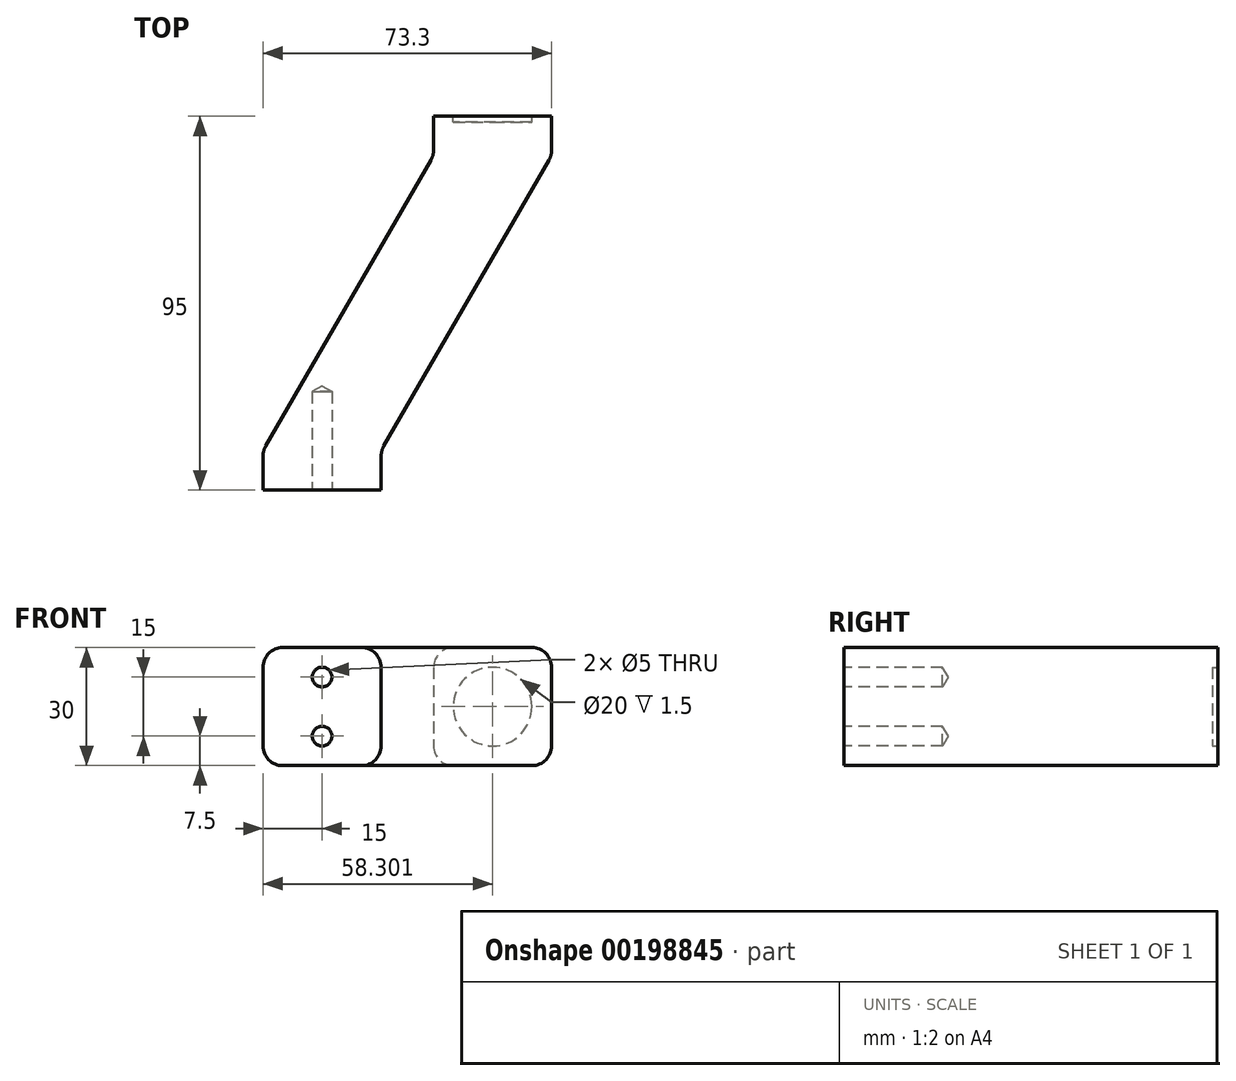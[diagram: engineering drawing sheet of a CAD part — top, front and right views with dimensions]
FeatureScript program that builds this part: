
annotation { "Feature Type Name" : "Feature", "Feature Type Description" : "" }
export const myFeature = defineFeature(function(context is Context, id is Id, definition is map)
    precondition{}
    {
        {
            var Q0;
            Q0=qCreatedBy(makeId("Top.planeOp"),FACE);
            var sketch = newSketch(context, id + "F0", { "sketchPlane" : qUnion([Q0])});
            skLineSegment(sketch, "E0.bottom", {"start": v(15, -5) * mm, "end": v(-15, -5) * mm});
            skLineSegment(sketch, "E0.top", {"start": v(15, 5) * mm, "end": v(-15, 5) * mm});
            skLineSegment(sketch, "E0.left", {"start": v(15, -5) * mm, "end": v(15, 5) * mm});
            skLineSegment(sketch, "E0.right", {"start": v(-15, -5) * mm, "end": v(-15, 5) * mm});
            skPoint(sketch, "E0.middle", {"position": v(0, 0) * mm});
            skLineSegment(sketch, "E1", {"start": v(15, 5) * mm, "end": v(58.3, 80) * mm});
            skLineSegment(sketch, "E2", {"start": v(-15, 5) * mm, "end": v(28.3, 80) * mm});
            skLineSegment(sketch, "E3.bottom", {"start": v(28.3, 80) * mm, "end": v(58.3, 80) * mm});
            skLineSegment(sketch, "E3.top", {"start": v(28.3, 90) * mm, "end": v(58.3, 90) * mm});
            skLineSegment(sketch, "E3.left", {"start": v(28.3, 80) * mm, "end": v(28.3, 90) * mm});
            skLineSegment(sketch, "E3.right", {"start": v(58.3, 80) * mm, "end": v(58.3, 90) * mm});
            skSolve(sketch);
        }
        {
            var Q0;
            Q0=makeQuery(id+"F0.imprint","IMPRINT",FACE,{"disambiguationData":[TD([[makeQuery(id+"F0.imprint","IMPRINT",EDGE,{"derivedFrom":sQuery(id+"F0.wireOp",EDGE,"E0.bottom")}),-1.0]])]});
            var Q1;
            Q1=makeQuery(id+"F0.imprint","IMPRINT",FACE,{"disambiguationData":[TD([[makeQuery(id+"F0.imprint","IMPRINT",EDGE,{"derivedFrom":sQuery(id+"F0.wireOp",EDGE,"E0.top")}),-1.0]])]});
            var Q2;
            Q2=makeQuery(id+"F0.imprint","IMPRINT",FACE,{"disambiguationData":[TD([[makeQuery(id+"F0.imprint","IMPRINT",EDGE,{"derivedFrom":sQuery(id+"F0.wireOp",EDGE,"E3.bottom")}),1.0]])]});
            extrude(context, id + "F1", {"entities" : qUnion([Q0, Q1, Q2]), "depth" : 30 * mm});
        }
        {
            var Q0;
            Q0=makeQuery(id+"F1.opExtrude","SWEPT_FACE",FACE,{"disambiguationData":[OSD([sQuery(id+"F0.wireOp",EDGE,"E0.bottom")])]});
            var sketch = newSketch(context, id + "F2", { "sketchPlane" : qUnion([Q0])});
            skPoint(sketch, "E4", {"position": v(0, 22.5) * mm});
            skPoint(sketch, "E4.positionSnap0", {"position": v(0, 30) * mm});
            skPoint(sketch, "E5", {"position": v(0, 7.5) * mm});
            skSolve(sketch);
        }
        {
            var Q0;
            Q0=sQuery(id+"F2.wireOp",VERTEX,"E4");
            var Q1;
            Q1=sQuery(id+"F2.wireOp",VERTEX,"E5");
            var Q2;
            Q2=makeQuery(id+"F1.opExtrude","SWEPT_BODY",BODY,{"disambiguationData":[OSD([sQuery(id+"F0.wireOp",EDGE,"E0.bottom"),sQuery(id+"F0.wireOp",EDGE,"E0.left"),sQuery(id+"F0.wireOp",EDGE,"E0.right"),sQuery(id+"F0.wireOp",EDGE,"E1"),sQuery(id+"F0.wireOp",EDGE,"E2"),sQuery(id+"F0.wireOp",EDGE,"E3.top"),sQuery(id+"F0.wireOp",EDGE,"E3.left"),sQuery(id+"F0.wireOp",EDGE,"E3.right")])]});
            hole(context, id + "F3", {"style" : HoleStyle.SIMPLE, "endStyle" : HoleEndStyle.BLIND, "holeDiameter" : 5 * mm, "holeDepth" : 25 * mm, "startFromSketch" : true, "locations" : qUnion([Q0, Q1]), "scope" : qUnion([Q2]), "tappedDepth" : 12 * mm, "tapClearance" : 3});
        }
        {
            var Q0;
            Q0=makeQuery(id+"F1.opExtrude","CAP_EDGE",EDGE,{"disambiguationData":[OSD([sQuery(id+"F0.wireOp",EDGE,"E0.left")])],"isStart":true});
            var Q1;
            Q1=makeQuery(id+"F1.opExtrude","CAP_EDGE",EDGE,{"disambiguationData":[OSD([sQuery(id+"F0.wireOp",EDGE,"E1")])],"isStart":true});
            var Q2;
            Q2=makeQuery(id+"F1.opExtrude","CAP_EDGE",EDGE,{"disambiguationData":[OSD([sQuery(id+"F0.wireOp",EDGE,"E0.left")])],"isStart":false});
            var Q3;
            Q3=makeQuery(id+"F1.opExtrude","CAP_EDGE",EDGE,{"disambiguationData":[OSD([sQuery(id+"F0.wireOp",EDGE,"E1")])],"isStart":false});
            var Q4;
            Q4=makeQuery(id+"F1.opExtrude","CAP_EDGE",EDGE,{"disambiguationData":[OSD([sQuery(id+"F0.wireOp",EDGE,"E0.right")])],"isStart":false});
            var Q5;
            Q5=makeQuery(id+"F1.opExtrude","CAP_EDGE",EDGE,{"disambiguationData":[OSD([sQuery(id+"F0.wireOp",EDGE,"E2")])],"isStart":false});
            var Q6;
            Q6=makeQuery(id+"F1.opExtrude","CAP_EDGE",EDGE,{"disambiguationData":[OSD([sQuery(id+"F0.wireOp",EDGE,"E3.left")])],"isStart":false});
            var Q7;
            Q7=makeQuery(id+"F1.opExtrude","CAP_EDGE",EDGE,{"disambiguationData":[OSD([sQuery(id+"F0.wireOp",EDGE,"E3.right")])],"isStart":false});
            var Q8;
            Q8=makeQuery(id+"F1.opExtrude","CAP_EDGE",EDGE,{"disambiguationData":[OSD([sQuery(id+"F0.wireOp",EDGE,"E3.right")])],"isStart":true});
            var Q9;
            Q9=makeQuery(id+"F1.opExtrude","CAP_EDGE",EDGE,{"disambiguationData":[OSD([sQuery(id+"F0.wireOp",EDGE,"E3.left")])],"isStart":true});
            var Q10;
            Q10=makeQuery(id+"F1.opExtrude","CAP_EDGE",EDGE,{"disambiguationData":[OSD([sQuery(id+"F0.wireOp",EDGE,"E2")])],"isStart":true});
            var Q11;
            Q11=makeQuery(id+"F1.opExtrude","CAP_EDGE",EDGE,{"disambiguationData":[OSD([sQuery(id+"F0.wireOp",EDGE,"E0.right")])],"isStart":true});
            var Q12;
            Q12=makeQuery(id+"F1.opExtrude","SWEPT_EDGE",EDGE,{"disambiguationData":[OSD([sQuery(id+"F0.wireOp",EDGE,"E1"),sQuery(id+"F0.wireOp",EDGE,"E3.bottom"),sQuery(id+"F0.wireOp",EDGE,"E3.right")])]});
            var Q13;
            Q13=makeQuery(id+"F1.opExtrude","SWEPT_EDGE",EDGE,{"disambiguationData":[OSD([sQuery(id+"F0.wireOp",EDGE,"E0.top"),sQuery(id+"F0.wireOp",EDGE,"E0.left"),sQuery(id+"F0.wireOp",EDGE,"E1")])]});
            var Q14;
            Q14=makeQuery(id+"F1.opExtrude","SWEPT_EDGE",EDGE,{"disambiguationData":[OSD([sQuery(id+"F0.wireOp",EDGE,"E0.top"),sQuery(id+"F0.wireOp",EDGE,"E0.right"),sQuery(id+"F0.wireOp",EDGE,"E2")])]});
            var Q15;
            Q15=makeQuery(id+"F1.opExtrude","SWEPT_EDGE",EDGE,{"disambiguationData":[OSD([sQuery(id+"F0.wireOp",EDGE,"E2"),sQuery(id+"F0.wireOp",EDGE,"E3.bottom"),sQuery(id+"F0.wireOp",EDGE,"E3.left")])]});
            fillet(context, id + "F4", {"entities" : qUnion([Q0, Q1, Q2, Q3, Q4, Q5, Q6, Q7, Q8, Q9, Q10, Q11, Q12, Q13, Q14, Q15]), "radius" : 5 * mm, "tangentPropagation" : true, "allowEdgeOverflow" : false});
        }
        {
            var Q0;
            Q0=makeQuery(id+"F1.opExtrude","SWEPT_FACE",FACE,{"disambiguationData":[OSD([sQuery(id+"F0.wireOp",EDGE,"E3.top")])]});
            var sketch = newSketch(context, id + "F5", { "sketchPlane" : qUnion([Q0])});
            skCircle(sketch, "E6", {"center": v(-43.3, 15) * mm, "radius": 10 * mm});
            skPoint(sketch, "E6.centerSnap0", {"position": v(-28.3, 15) * mm});
            skPoint(sketch, "E6.centerSnap1", {"position": v(-43.3, 30) * mm});
            skSolve(sketch);
        }
        {
            var Q0;
            Q0=makeQuery(id+"F5.imprint","IMPRINT",FACE,{"disambiguationData":[TD([[makeQuery(id+"F5.imprint","IMPRINT",EDGE,{"derivedFrom":sQuery(id+"F5.wireOp",EDGE,"E6")}),1.0]])]});
            extrude(context, id + "F6", {"entities" : qUnion([Q0]), "operationType" : NewBodyOperationType.REMOVE, "oppositeDirection" : true, "depth" : 1.5 * mm});
        }
    });
